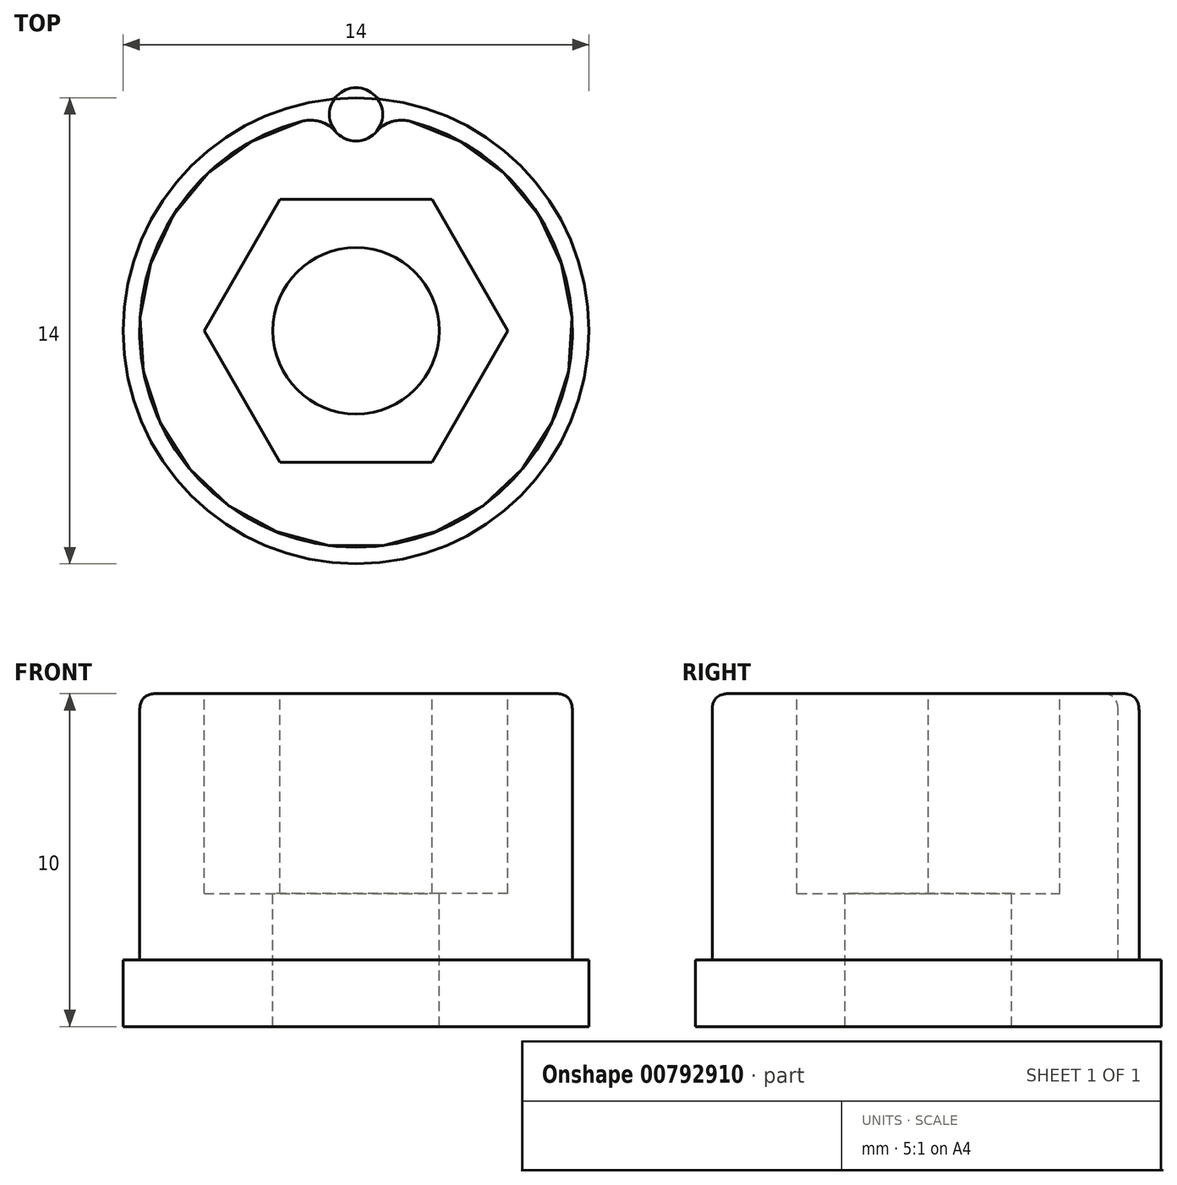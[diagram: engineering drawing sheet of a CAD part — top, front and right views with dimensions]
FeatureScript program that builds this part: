
annotation { "Feature Type Name" : "Feature", "Feature Type Description" : "" }
export const myFeature = defineFeature(function(context is Context, id is Id, definition is map)
    precondition{}
    {
        {
            var Q0;
            Q0=qCreatedBy(makeId("Top.planeOp"),FACE);
            var sketch = newSketch(context, id + "F0", { "sketchPlane" : qUnion([Q0])});
            skCircle(sketch, "E0", {"center": v(0, 0) * mm, "radius": 7 * mm});
            skSolve(sketch);
        }
        {
            var Q0;
            Q0 = qSketchRegion(id + "F0", true);
            extrude(context, id + "F1", {"entities" : qUnion([Q0]), "depth" : 2 * mm, "offsetDistance" : 25 * mm});
        }
        {
            var Q0;
            Q0=makeQuery(id+"F1.opExtrude","CAP_FACE",FACE,{"disambiguationData":[OSD([sQuery(id+"F0.wireOp",EDGE,"E0")])],"isStart":false});
            var sketch = newSketch(context, id + "F2", { "sketchPlane" : qUnion([Q0])});
            skCircle(sketch, "E1", {"center": v(0, 0) * mm, "radius": 6.5 * mm});
            skSolve(sketch);
        }
        {
            var Q0;
            Q0 = qSketchRegion(id + "F2", true);
            extrude(context, id + "F3", {"entities" : qUnion([Q0]), "operationType" : NewBodyOperationType.ADD, "depth" : 8 * mm, "offsetDistance" : 25 * mm});
        }
        {
            var Q0;
            Q0=makeQuery(id+"F3.opExtrude","CAP_FACE",FACE,{"disambiguationData":[OSD([sQuery(id+"F2.wireOp",EDGE,"E1")])],"isStart":false});
            var sketch = newSketch(context, id + "F4", { "sketchPlane" : qUnion([Q0])});
            skCircle(sketch, "E2", {"center": v(0, 6.5) * mm, "radius": 0.8 * mm});
            skSolve(sketch);
        }
        {
            var Q0;
            Q0 = qSketchRegion(id + "F4", true);
            var Q1;
            Q1=makeQuery(id+"F1.opExtrude","CAP_FACE",FACE,{"disambiguationData":[OSD([sQuery(id+"F0.wireOp",EDGE,"E0")])],"isStart":false});
            extrude(context, id + "F5", {"entities" : qUnion([Q0]), "operationType" : NewBodyOperationType.REMOVE, "endBound" : BoundingType.UP_TO_SURFACE, "oppositeDirection" : true, "depth" : 25 * mm, "endBoundEntityFace" : qUnion([Q1]), "offsetDistance" : 25 * mm});
        }
        {
            var Q0;
            Q0=makeQuery(id+"F5.boolean.opBoolean","INTERSECT",EDGE,{"disambiguationData":[OD(0.0)],"derivedFrom":[makeQuery(id+"F3.opExtrude","SWEPT_FACE",FACE,{"disambiguationData":[OSD([sQuery(id+"F2.wireOp",EDGE,"E1")])]}),makeQuery(id+"F5.opExtrude","SWEPT_FACE",FACE,{"disambiguationData":[OSD([sQuery(id+"F4.wireOp",EDGE,"E2")])]})]});
            var Q1;
            Q1=makeQuery(id+"F5.boolean.opBoolean","INTERSECT",EDGE,{"disambiguationData":[OD(1.0)],"derivedFrom":[makeQuery(id+"F3.opExtrude","SWEPT_FACE",FACE,{"disambiguationData":[OSD([sQuery(id+"F2.wireOp",EDGE,"E1")])]}),makeQuery(id+"F5.opExtrude","SWEPT_FACE",FACE,{"disambiguationData":[OSD([sQuery(id+"F4.wireOp",EDGE,"E2")])]})]});
            fillet(context, id + "F6", {"entities" : qUnion([Q0, Q1]), "radius" : 1 * mm, "tangentPropagation" : true, "allowEdgeOverflow" : false});
        }
        {
            var Q0;
            Q0=makeQuery(id+"F3.opExtrude","CAP_FACE",FACE,{"disambiguationData":[OSD([sQuery(id+"F2.wireOp",EDGE,"E1")])],"isStart":false});
            fillet(context, id + "F7", {"entities" : qUnion([Q0]), "radius" : .5 * mm, "tangentPropagation" : true, "rho" : 0.5, "crossSection" : FilletCrossSection.CONIC, "allowEdgeOverflow" : false});
        }
        {
            var Q0;
            Q0=makeQuery(id+"F3.opExtrude","CAP_FACE",FACE,{"disambiguationData":[OSD([sQuery(id+"F2.wireOp",EDGE,"E1")])],"isStart":false});
            var sketch = newSketch(context, id + "F8", { "sketchPlane" : qUnion([Q0])});
            skCircle(sketch, "E3.cCircle", {"center": v(0, 0) * mm, "radius": 3.95 * mm, "construction": true});
            skLineSegment(sketch, "E3.0", {"start": v(-2.28, 3.95) * mm, "end": v(2.28, 3.95) * mm});
            skLineSegment(sketch, "E3.1", {"start": v(2.28, 3.95) * mm, "end": v(4.56, 0) * mm});
            skLineSegment(sketch, "E3.2", {"start": v(4.56, 0) * mm, "end": v(2.28, -3.95) * mm});
            skLineSegment(sketch, "E3.3", {"start": v(2.28, -3.95) * mm, "end": v(-2.28, -3.95) * mm});
            skLineSegment(sketch, "E3.4", {"start": v(-2.28, -3.95) * mm, "end": v(-4.56, 0) * mm});
            skLineSegment(sketch, "E3.5", {"start": v(-4.56, 0) * mm, "end": v(-2.28, 3.95) * mm});
            skPoint(sketch, "E3.0.midPoint", {"position": v(0, 3.95) * mm});
            skSolve(sketch);
        }
        {
            var Q0;
            Q0 = qSketchRegion(id + "F8", true);
            extrude(context, id + "F9", {"entities" : qUnion([Q0]), "operationType" : NewBodyOperationType.REMOVE, "oppositeDirection" : true, "depth" : 6 * mm, "offsetDistance" : 25 * mm});
        }
        {
            var Q0;
            Q0=makeQuery(id+"F9.boolean.opBoolean","COPY",FACE,{"derivedFrom":makeQuery(id+"F9.opExtrude","CAP_FACE",FACE,{"disambiguationData":[OSD([sQuery(id+"F8.wireOp",EDGE,"E3.0"),sQuery(id+"F8.wireOp",EDGE,"E3.1"),sQuery(id+"F8.wireOp",EDGE,"E3.2"),sQuery(id+"F8.wireOp",EDGE,"E3.3"),sQuery(id+"F8.wireOp",EDGE,"E3.4"),sQuery(id+"F8.wireOp",EDGE,"E3.5")])],"isStart":false})});
            var sketch = newSketch(context, id + "F10", { "sketchPlane" : qUnion([Q0])});
            skCircle(sketch, "E4", {"center": v(0, 0) * mm, "radius": 2.5 * mm});
            skSolve(sketch);
        }
        {
            var Q0;
            Q0 = qSketchRegion(id + "F10", true);
            extrude(context, id + "F11", {"entities" : qUnion([Q0]), "operationType" : NewBodyOperationType.REMOVE, "endBound" : BoundingType.THROUGH_ALL, "oppositeDirection" : true, "depth" : 25 * mm, "offsetDistance" : 25 * mm});
        }
    });
